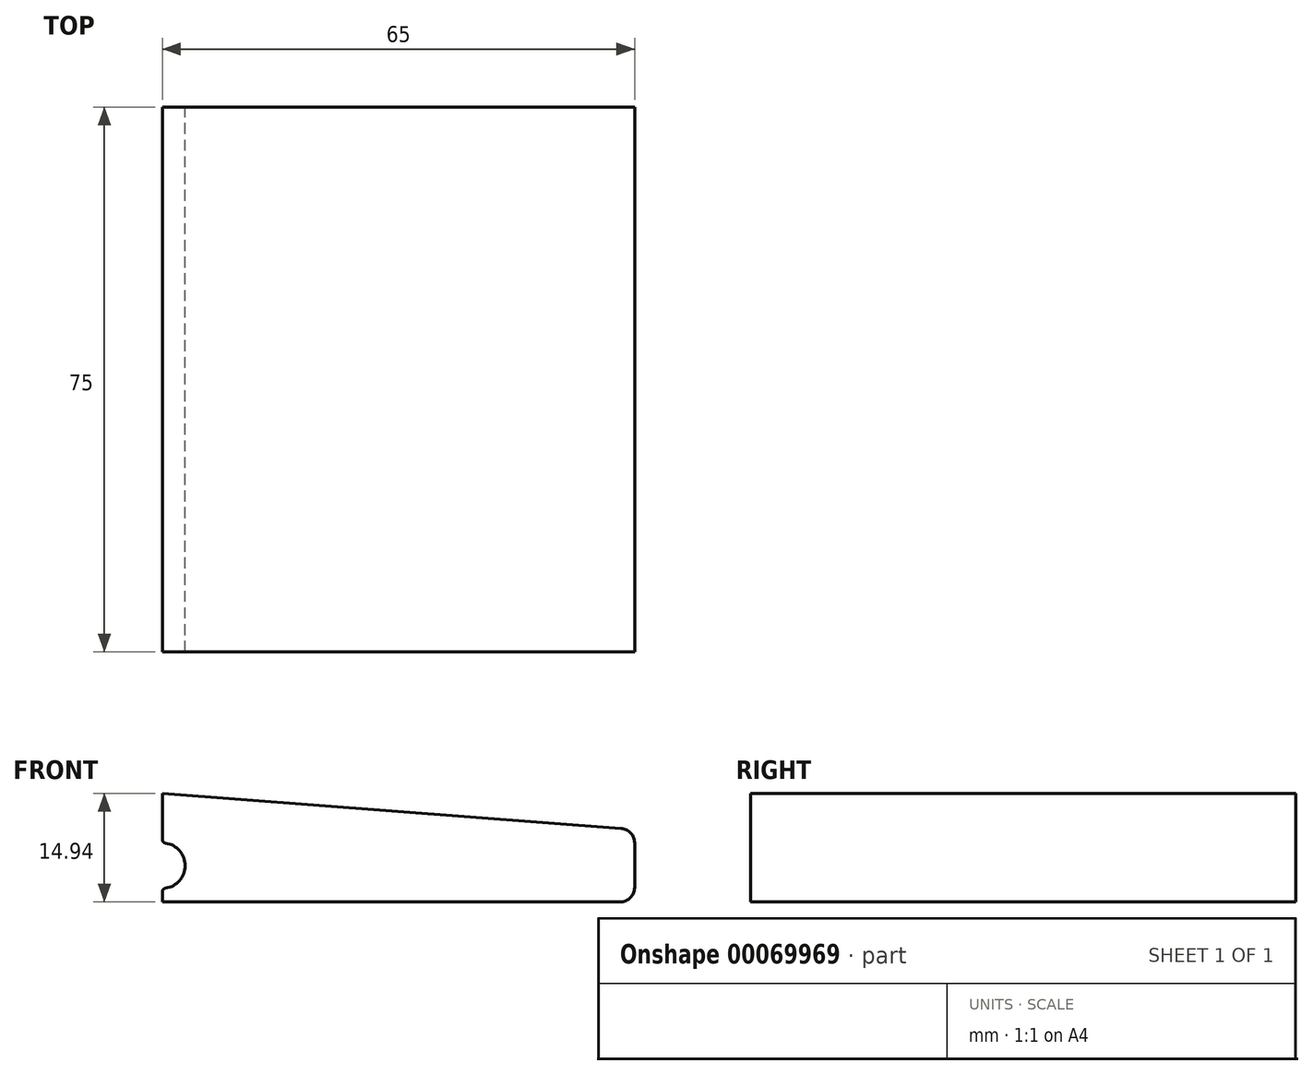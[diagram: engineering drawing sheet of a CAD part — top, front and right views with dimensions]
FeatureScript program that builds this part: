
annotation { "Feature Type Name" : "Feature", "Feature Type Description" : "" }
export const myFeature = defineFeature(function(context is Context, id is Id, definition is map)
    precondition{}
    {
        {
            var Q0;
            Q0=qCreatedBy(makeId("Front.planeOp"),FACE);
            var sketch = newSketch(context, id + "F0", { "sketchPlane" : qUnion([Q0])});
            skLineSegment(sketch, "E0.top", {"start": v(46.7, 0) * mm, "end": v(-16.3, 0) * mm});
            skArc(sketch, "E1", {"start": v(-15.88, 1.91) * mm, "mid": v(-13.18, 5) * mm, "end": v(-15.88, 8.1) * mm});
            skLineSegment(sketch, "E2.trimOffspring", {"start": v(-16.3, 1.42) * mm, "end": v(-16.3, 0) * mm});
            skPoint(sketch, "E3.visualSharp", {"position": v(-16.3, 8.13) * mm});
            skArc(sketch, "E3.filletArc", {"start": v(-16.3, 8.6) * mm, "mid": v(-16.18, 8.27) * mm, "end": v(-15.88, 8.1) * mm});
            skPoint(sketch, "E4.visualSharp", {"position": v(-16.3, 1.88) * mm});
            skArc(sketch, "E4.filletArc", {"start": v(-15.88, 1.91) * mm, "mid": v(-16.18, 1.75) * mm, "end": v(-16.3, 1.42) * mm});
            skLineSegment(sketch, "E5", {"start": v(-16.3, 8.6) * mm, "end": v(-16.3, 14.95) * mm});
            skLineSegment(sketch, "E6", {"start": v(48.7, 2) * mm, "end": v(48.7, 8.15) * mm});
            skLineSegment(sketch, "E7", {"start": v(-16.3, 14.95) * mm, "end": v(46.84, 10.15) * mm});
            skPoint(sketch, "E8.visualSharp", {"position": v(48.7, 10) * mm});
            skArc(sketch, "E8.filletArc", {"start": v(48.7, 8.15) * mm, "mid": v(48.16, 9.51) * mm, "end": v(46.84, 10.15) * mm});
            skPoint(sketch, "E9.visualSharp", {"position": v(48.7, 0) * mm});
            skArc(sketch, "E9.filletArc", {"start": v(46.7, 0) * mm, "mid": v(48.1, 0.6) * mm, "end": v(48.7, 2) * mm});
            skSolve(sketch);
        }
        {
            var Q0;
            Q0 = qSketchRegion(id + "F0", true);
            extrude(context, id + "F1", {"entities" : qUnion([Q0]), "depth" : 75 * mm});
        }
    });
